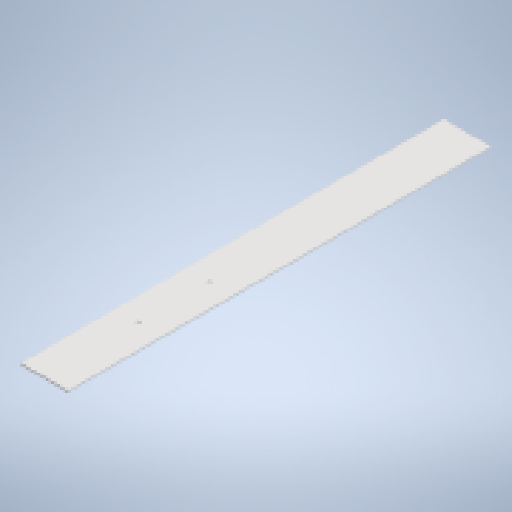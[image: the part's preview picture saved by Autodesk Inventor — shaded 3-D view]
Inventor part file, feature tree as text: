
AUTODESK INVENTOR PART (.ipt)
format: ipt  version: 2023 (Build 270158000, 158)  size: 140,800 bytes
history: native  units: mm
features: extrude x1, sketch x1
ambient origin geometry x8: Origin, YZ Plane, XZ Plane, XY Plane, X Axis, Y Axis, Z Axis, Center Point
bodies: Body1 (feature_tree)
feature tree (2):
  extrude  "Extrusion2"  Depth=450.0mm
  sketch  "Sketch1"  dims[d0=50.0mm d1=450.0mm d6=100.0mm d7=5.0mm d8=75.0mm d9=5.0mm d10=2.0mm d11=0.0mm]
